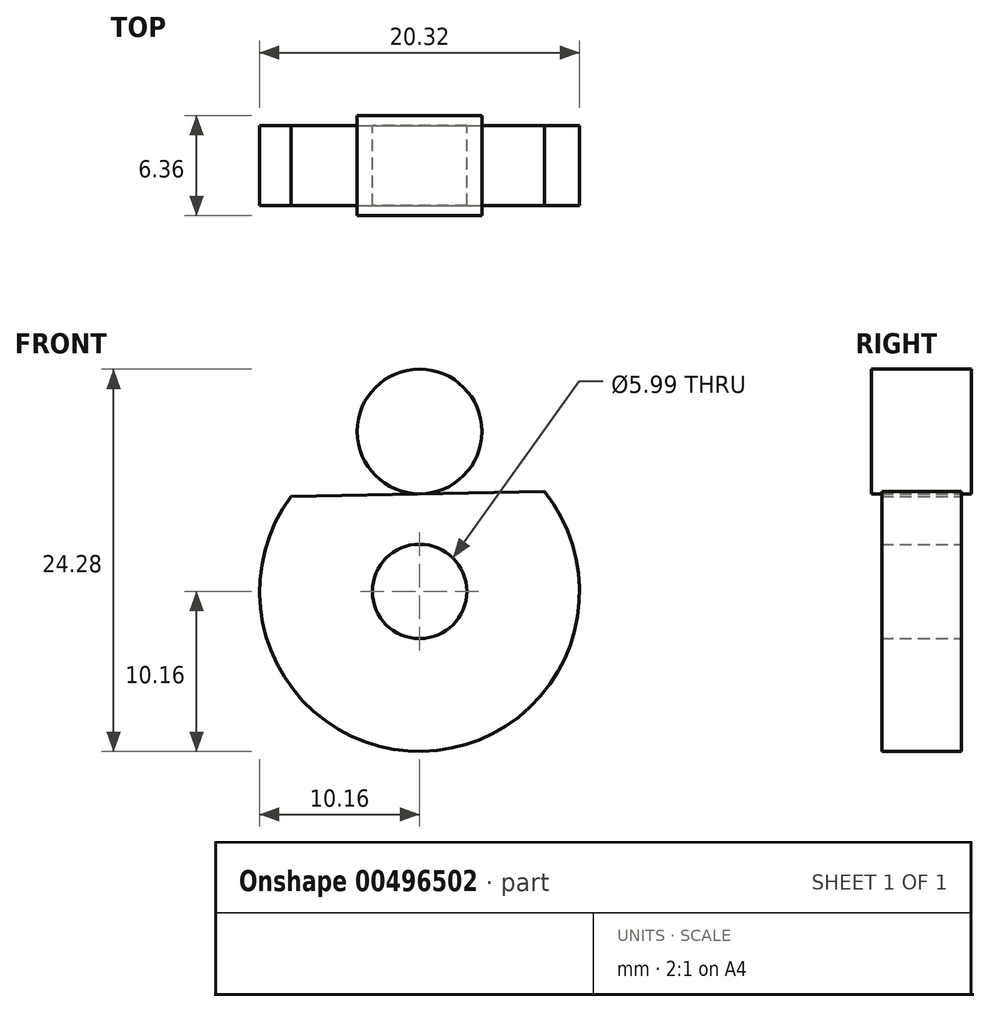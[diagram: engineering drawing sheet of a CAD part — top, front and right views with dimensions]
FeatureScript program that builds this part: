
annotation { "Feature Type Name" : "Feature", "Feature Type Description" : "" }
export const myFeature = defineFeature(function(context is Context, id is Id, definition is map)
    precondition{}
    {
        {
            var Q0;
            Q0=qCreatedBy(makeId("Front.planeOp"),FACE);
            var sketch = newSketch(context, id + "F0", { "sketchPlane" : qUnion([Q0])});
            skCircle(sketch, "E0", {"center": v(0, 0) * mm, "radius": 3 * mm});
            skPoint(sketch, "E1", {"position": v(0, 10.16) * mm});
            skArc(sketch, "E2", {"start": v(-8.17, 6.04) * mm, "mid": v(0.2, -10.16) * mm, "end": v(7.93, 6.35) * mm});
            skLineSegment(sketch, "E3", {"start": v(-8.17, 6.04) * mm, "end": v(7.93, 6.35) * mm});
            skCircle(sketch, "E4", {"center": v(0, 10.16) * mm, "radius": 3.96 * mm});
            skSolve(sketch);
        }
        {
            var Q0;
            Q0=makeQuery(id+"F0.imprint","IMPRINT",FACE,{"disambiguationData":[TD([[makeQuery(id+"F0.imprint","IMPRINT",EDGE,{"derivedFrom":sQuery(id+"F0.wireOp",EDGE,"E0")}),-1.0]])]});
            extrude(context, id + "F1", {"entities" : qUnion([Q0]), "endBound" : BoundingType.SYMMETRIC, "depth" : 5.08 * mm});
        }
        {
            var Q0;
            {var subQ0=sQuery(id+"F0.wireOp",EDGE,"lrpbFcvU-aWWu-lmA1-OamQ-iTll7kNaeCtg");var subQ1=sQuery(id+"F0.wireOp",EDGE,"E3");var subQ2=makeQuery(id+"F0.imprint","INTERSECT",VERTEX,{"disambiguationData":[OD(0.0)],"derivedFrom":[subQ1,subQ0]});Q0=makeQuery(id+"F0.imprint","IMPRINT",FACE,{"disambiguationData":[TD([[makeQuery(id+"F0.imprint","IMPRINT",EDGE,{"disambiguationData":[TD([[subQ2,-1.0]])],"derivedFrom":subQ1}),1.0]])]});}
            var Q1;
            Q1=makeQuery(id+"F0.imprint","IMPRINT",FACE,{"disambiguationData":[TD([[makeQuery(id+"F0.imprint","IMPRINT",EDGE,{"derivedFrom":sQuery(id+"F0.wireOp",EDGE,"E4")}),1.0]])]});
            extrude(context, id + "F2", {"entities" : qUnion([Q0, Q1]), "endBound" : BoundingType.SYMMETRIC, "depth" : 6.35 * mm});
        }
    });
